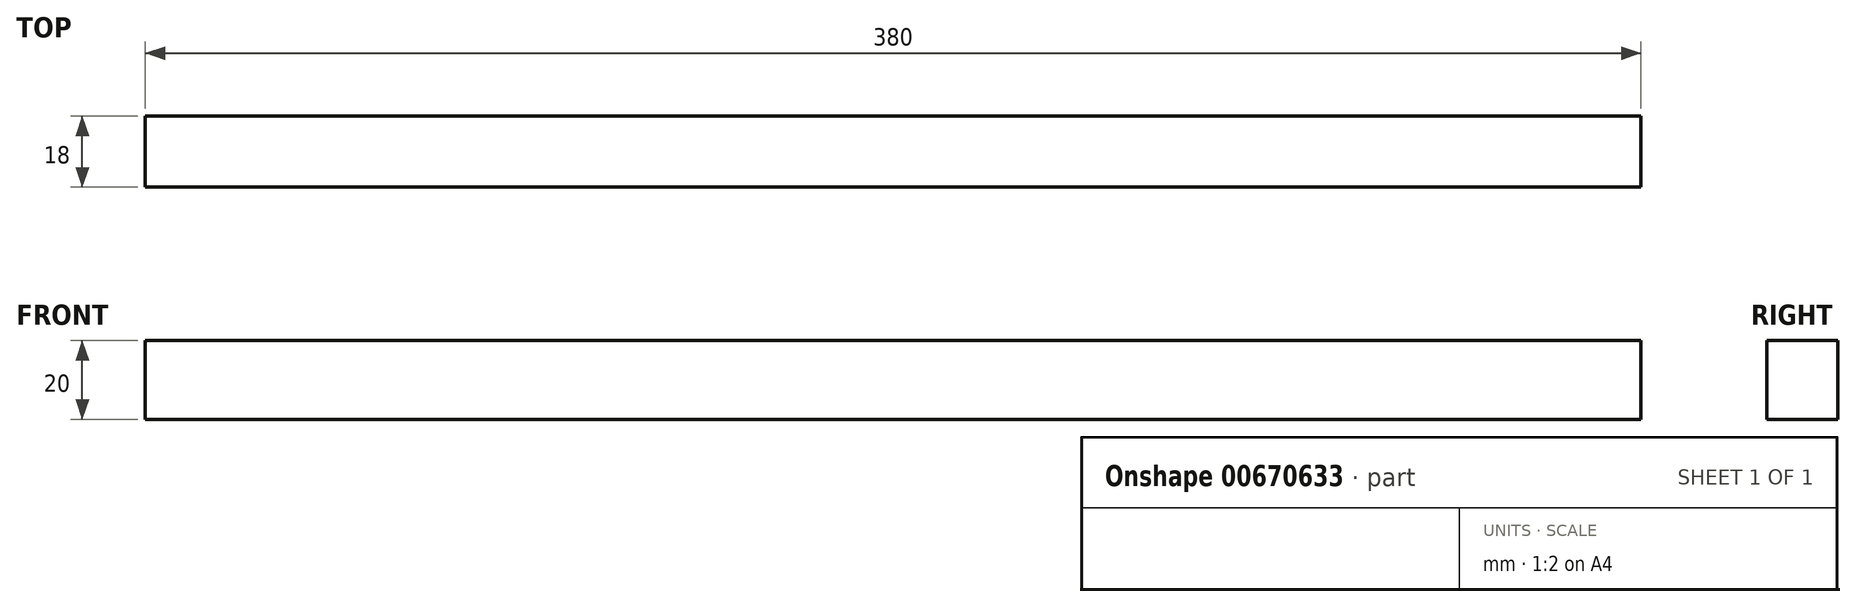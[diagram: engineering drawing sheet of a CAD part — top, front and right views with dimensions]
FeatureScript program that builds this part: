
annotation { "Feature Type Name" : "Feature", "Feature Type Description" : "" }
export const myFeature = defineFeature(function(context is Context, id is Id, definition is map)
    precondition{}
    {
        {
            var Q0;
            Q0=qCreatedBy(makeId("Top.planeOp"),FACE);
            var sketch = newSketch(context, id + "F0", { "sketchPlane" : qUnion([Q0])});
            skLineSegment(sketch, "E0.bottom", {"start": v(190, 9) * mm, "end": v(-190, 9) * mm});
            skLineSegment(sketch, "E0.top", {"start": v(190, -9) * mm, "end": v(-190, -9) * mm});
            skLineSegment(sketch, "E0.left", {"start": v(190, 9) * mm, "end": v(190, -9) * mm});
            skLineSegment(sketch, "E0.right", {"start": v(-190, 9) * mm, "end": v(-190, -9) * mm});
            skPoint(sketch, "E0.middle", {"position": v(0, 0) * mm});
            skSolve(sketch);
        }
        {
            var Q0;
            Q0 = qSketchRegion(id + "F0", true);
            extrude(context, id + "F1", {"entities" : qUnion([Q0]), "endBound" : BoundingType.SYMMETRIC, "depth" : 20 * mm, "offsetDistance" : 25 * mm});
        }
    });
